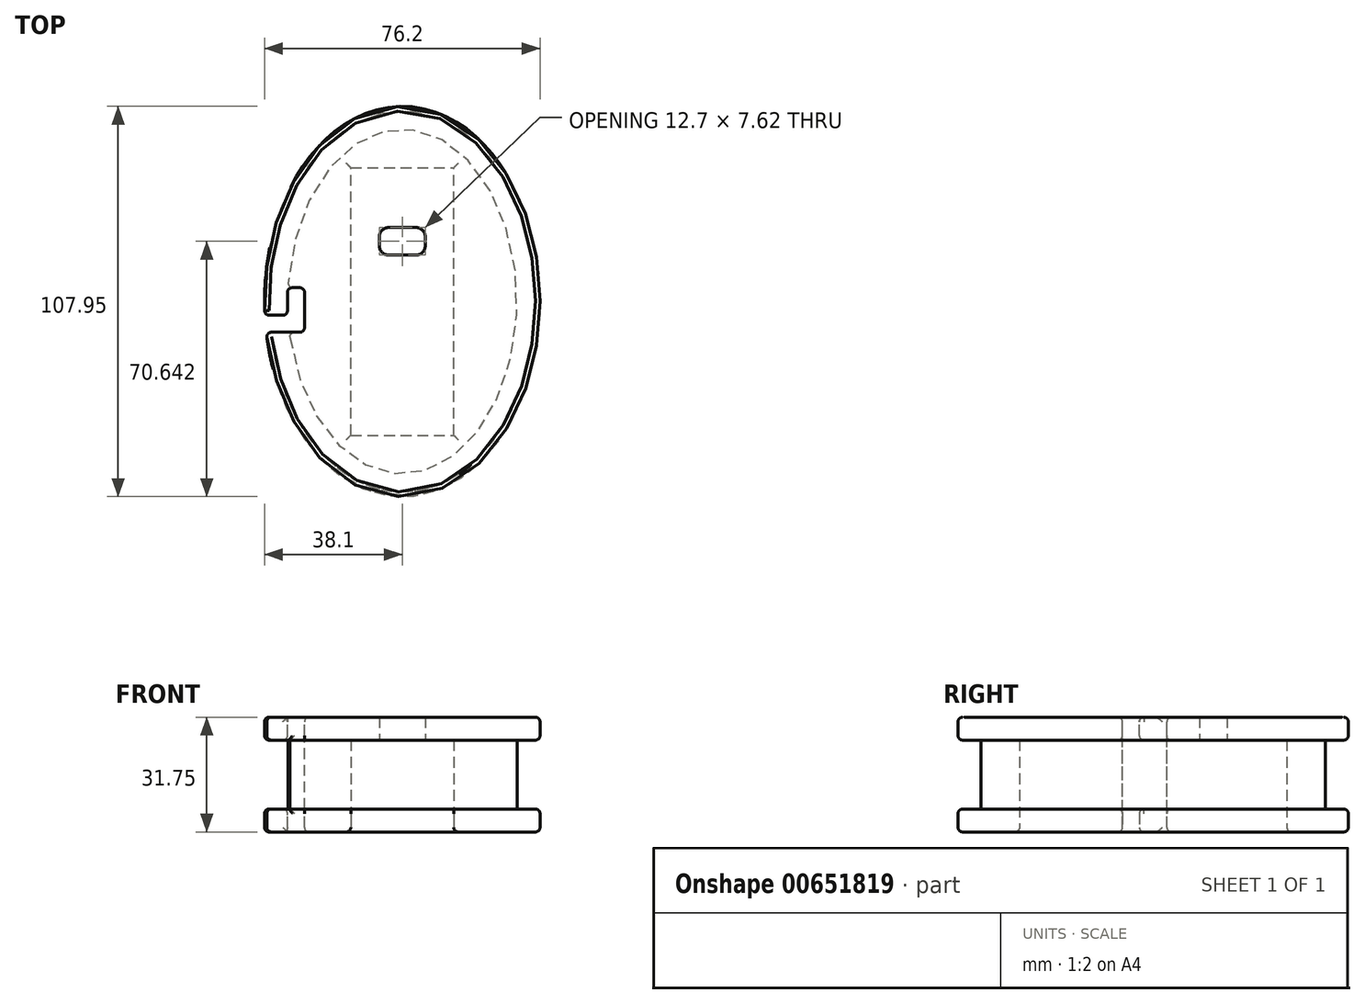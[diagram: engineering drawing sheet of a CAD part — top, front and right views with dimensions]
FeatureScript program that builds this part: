
annotation { "Feature Type Name" : "Feature", "Feature Type Description" : "" }
export const myFeature = defineFeature(function(context is Context, id is Id, definition is map)
    precondition{}
    {
        {
            var Q0;
            Q0=qCreatedBy(makeId("Top.planeOp"),FACE);
            var sketch = newSketch(context, id + "F0", { "sketchPlane" : qUnion([Q0])});
            skLineSegment(sketch, "E0.bottom", {"start": v(-14.24, -36.98) * mm, "end": v(14.24, -36.98) * mm});
            skLineSegment(sketch, "E0.top", {"start": v(-14.24, 36.98) * mm, "end": v(14.24, 36.98) * mm});
            skLineSegment(sketch, "E0.left", {"start": v(-14.24, -36.98) * mm, "end": v(-14.24, 36.98) * mm});
            skLineSegment(sketch, "E0.right", {"start": v(14.24, -36.98) * mm, "end": v(14.24, 36.98) * mm});
            skEllipse(sketch, "E1", {"center": v(0, 0) * mm, "majorRadius": 47.63 * mm, "minorRadius": 31.75 * mm, "majorAxis": v(0, 1)});
            skSolve(sketch);
        }
        {
            var Q0;
            Q0=makeQuery(id+"F0.imprint","IMPRINT",FACE,{"disambiguationData":[TD([[makeQuery(id+"F0.imprint","IMPRINT",EDGE,{"derivedFrom":sQuery(id+"F0.wireOp",EDGE,"E0.bottom")}),-1.0]])]});
            extrude(context, id + "F1", {"entities" : qUnion([Q0]), "depth" : 25.4 * mm, "offsetDistance" : 25.4 * mm});
        }
        {
            var Q0;
            Q0=makeQuery(id+"F1.opExtrude","CAP_FACE",FACE,{"disambiguationData":[OSD([sQuery(id+"F0.wireOp",EDGE,"E0.bottom"),sQuery(id+"F0.wireOp",EDGE,"E0.top"),sQuery(id+"F0.wireOp",EDGE,"E0.left"),sQuery(id+"F0.wireOp",EDGE,"E0.right"),sQuery(id+"F0.wireOp",EDGE,"E1")])],"isStart":false});
            var sketch = newSketch(context, id + "F2", { "sketchPlane" : qUnion([Q0])});
            skEllipse(sketch, "E2", {"center": v(0, 0) * mm, "majorRadius": 53.98 * mm, "minorRadius": 38.1 * mm, "majorAxis": v(0, -1)});
            skSolve(sketch);
        }
        {
            var Q0;
            Q0=makeQuery(id+"F2.imprint","IMPRINT",FACE,{"disambiguationData":[TD([[makeQuery(id+"F2.imprint","IMPRINT",EDGE,{"derivedFrom":sQuery(id+"F2.wireOp",EDGE,"E2")}),1.0]])]});
            var Q1;
            Q1=makeQuery(id+"F2.imprint","IMPRINT",FACE,{"disambiguationData":[TD([[makeQuery(id+"F2.imprint","IMPRINT",EDGE,{"derivedFrom":makeQuery(id+"F1.opExtrude","CAP_EDGE",EDGE,{"disambiguationData":[OSD([sQuery(id+"F0.wireOp",EDGE,"E0.bottom")])],"isStart":false})}),-1.0]])]});
            var Q2;
            Q2=makeQuery(id+"F2.imprint","IMPRINT",FACE,{"disambiguationData":[TD([[makeQuery(id+"F2.imprint","IMPRINT",EDGE,{"derivedFrom":makeQuery(id+"F1.opExtrude","CAP_EDGE",EDGE,{"disambiguationData":[OSD([sQuery(id+"F0.wireOp",EDGE,"E0.bottom")])],"isStart":false})}),1.0]])]});
            extrude(context, id + "F3", {"entities" : qUnion([Q0, Q1, Q2]), "operationType" : NewBodyOperationType.ADD, "depth" : 6.35 * mm, "offsetDistance" : 25.4 * mm});
        }
        {
            var Q0;
            Q0=makeQuery(id+"F1.opExtrude","CAP_FACE",FACE,{"disambiguationData":[OSD([sQuery(id+"F0.wireOp",EDGE,"E0.bottom"),sQuery(id+"F0.wireOp",EDGE,"E0.top"),sQuery(id+"F0.wireOp",EDGE,"E0.left"),sQuery(id+"F0.wireOp",EDGE,"E0.right"),sQuery(id+"F0.wireOp",EDGE,"E1")])],"isStart":true});
            var sketch = newSketch(context, id + "F4", { "sketchPlane" : qUnion([Q0])});
            skEllipse(sketch, "E3", {"center": v(0, 0) * mm, "majorRadius": 53.98 * mm, "minorRadius": 38.1 * mm, "majorAxis": v(0, 1)});
            skSolve(sketch);
        }
        {
            var Q0;
            Q0=makeQuery(id+"F4.imprint","IMPRINT",FACE,{"disambiguationData":[TD([[makeQuery(id+"F4.imprint","IMPRINT",EDGE,{"derivedFrom":sQuery(id+"F4.wireOp",EDGE,"E3")}),1.0]])]});
            extrude(context, id + "F5", {"entities" : qUnion([Q0]), "operationType" : NewBodyOperationType.ADD, "oppositeDirection" : true, "depth" : 6.35 * mm, "offsetDistance" : 25.4 * mm});
        }
        {
            var Q0;
            Q0=makeQuery(id+"F5.opExtrude","CAP_EDGE",EDGE,{"disambiguationData":[OSD([sQuery(id+"F4.wireOp",EDGE,"E3")])],"isStart":true});
            var Q1;
            Q1=makeQuery(id+"F5.opExtrude","CAP_EDGE",EDGE,{"disambiguationData":[OSD([sQuery(id+"F4.wireOp",EDGE,"E3")])],"isStart":false});
            var Q2;
            Q2=makeQuery(id+"F3.opExtrude","CAP_EDGE",EDGE,{"disambiguationData":[OSD([sQuery(id+"F2.wireOp",EDGE,"E2")])],"isStart":true});
            var Q3;
            Q3=makeQuery(id+"F3.opExtrude","CAP_EDGE",EDGE,{"disambiguationData":[OSD([sQuery(id+"F2.wireOp",EDGE,"E2")])],"isStart":false});
            fillet(context, id + "F6", {"entities" : qUnion([Q0, Q1, Q2, Q3]), "radius" : 1.27 * mm, "tangentPropagation" : true, "allowEdgeOverflow" : false});
        }
        {
            var Q0;
            Q0=makeQuery(id+"F1.opExtrude","CAP_EDGE",EDGE,{"disambiguationData":[OSD([sQuery(id+"F0.wireOp",EDGE,"E0.left")])],"isStart":true});
            var Q1;
            Q1=makeQuery(id+"F1.opExtrude","CAP_EDGE",EDGE,{"disambiguationData":[OSD([sQuery(id+"F0.wireOp",EDGE,"E0.bottom")])],"isStart":true});
            var Q2;
            Q2=makeQuery(id+"F1.opExtrude","CAP_EDGE",EDGE,{"disambiguationData":[OSD([sQuery(id+"F0.wireOp",EDGE,"E0.right")])],"isStart":true});
            var Q3;
            Q3=makeQuery(id+"F1.opExtrude","CAP_EDGE",EDGE,{"disambiguationData":[OSD([sQuery(id+"F0.wireOp",EDGE,"E0.top")])],"isStart":true});
            fillet(context, id + "F7", {"entities" : qUnion([Q0, Q1, Q2, Q3]), "radius" : 1.27 * mm, "tangentPropagation" : true, "allowEdgeOverflow" : false});
        }
        {
            var Q0;
            Q0=makeQuery(id+"F3.opExtrude","CAP_FACE",FACE,{"disambiguationData":[OSD([sQuery(id+"F2.wireOp",EDGE,"E2")])],"isStart":false});
            var sketch = newSketch(context, id + "F8", { "sketchPlane" : qUnion([Q0])});
            skLineSegment(sketch, "E4", {"start": v(-42.58, -3.81) * mm, "end": v(-31.75, -3.81) * mm});
            skLineSegment(sketch, "E5", {"start": v(-31.75, -3.81) * mm, "end": v(-31.75, 3.81) * mm});
            skLineSegment(sketch, "E6", {"start": v(-31.75, 3.81) * mm, "end": v(-27.05, 3.81) * mm});
            skLineSegment(sketch, "E7", {"start": v(-27.05, 3.81) * mm, "end": v(-27.05, -8.5) * mm});
            skLineSegment(sketch, "E8", {"start": v(-27.05, -8.5) * mm, "end": v(-42.58, -8.5) * mm});
            skLineSegment(sketch, "E9", {"start": v(-42.58, -8.5) * mm, "end": v(-42.58, -3.81) * mm});
            skSolve(sketch);
        }
        {
            var Q0;
            {var subQ1=sQuery(id+"F8.wireOp",EDGE,"E5");Q0=makeQuery(id+"F8.imprint","IMPRINT",FACE,{"disambiguationData":[TD([[makeQuery(id+"F8.imprint","IMPRINT",EDGE,{"derivedFrom":subQ1}),-1.0]])]});}
            var Q1;
            {var subQ0=sQuery(id+"F8.wireOp",EDGE,"E9");Q1=makeQuery(id+"F8.imprint","IMPRINT",FACE,{"disambiguationData":[TD([[makeQuery(id+"F8.imprint","IMPRINT",EDGE,{"derivedFrom":subQ0}),-1.0]])]});}
            extrude(context, id + "F9", {"entities" : qUnion([Q0, Q1]), "operationType" : NewBodyOperationType.REMOVE, "oppositeDirection" : true, "depth" : 31.75 * mm, "offsetDistance" : 25.4 * mm});
        }
        {
            var Q0;
            Q0=makeQuery(id+"F9.boolean.opBoolean","COPY",EDGE,{"derivedFrom":makeQuery(id+"F9.opExtrude","SWEPT_EDGE",EDGE,{"disambiguationData":[OSD([sQuery(id+"F8.wireOp",EDGE,"E6"),sQuery(id+"F8.wireOp",EDGE,"E7")])]})});
            var Q1;
            Q1=makeQuery(id+"F9.boolean.opBoolean","COPY",EDGE,{"derivedFrom":makeQuery(id+"F9.opExtrude","SWEPT_EDGE",EDGE,{"disambiguationData":[OSD([sQuery(id+"F8.wireOp",EDGE,"E7"),sQuery(id+"F8.wireOp",EDGE,"E8")])]})});
            var Q2;
            Q2=makeQuery(id+"F9.boolean.opBoolean","INTERSECT",EDGE,{"derivedFrom":[makeQuery(id+"F1.opExtrude","SWEPT_FACE",FACE,{"disambiguationData":[OSD([sQuery(id+"F0.wireOp",EDGE,"E1")])]}),makeQuery(id+"F9.opExtrude","SWEPT_FACE",FACE,{"disambiguationData":[OSD([sQuery(id+"F8.wireOp",EDGE,"E8")])]})]});
            var Q3;
            Q3=makeQuery(id+"F9.boolean.opBoolean","INTERSECT",EDGE,{"derivedFrom":[makeQuery(id+"F1.opExtrude","SWEPT_FACE",FACE,{"disambiguationData":[OSD([sQuery(id+"F0.wireOp",EDGE,"E1")])]}),makeQuery(id+"F9.opExtrude","SWEPT_FACE",FACE,{"disambiguationData":[OSD([sQuery(id+"F8.wireOp",EDGE,"E6")])]})]});
            fillet(context, id + "F10", {"entities" : qUnion([Q0, Q1, Q2, Q3]), "radius" : 1.27 * mm, "tangentPropagation" : true, "allowEdgeOverflow" : false});
        }
        {
            var Q0;
            {var subQ0=sQuery(id+"F4.wireOp",EDGE,"E3");var subQ1=sQuery(id+"F0.wireOp",EDGE,"E1");var subQ2=sQuery(id+"F8.wireOp",EDGE,"E4");var subQ3=sQuery(id+"F8.wireOp",EDGE,"E5");Q0=makeQuery(id+"F9.boolean.opBoolean","COPY",EDGE,{"disambiguationData":[TD([makeQuery(id+"F5.opExtrude","CAP_FACE",FACE,{"disambiguationData":[OSD([subQ1,subQ0])],"isStart":true})])],"derivedFrom":makeQuery(id+"F9.opExtrude","SWEPT_EDGE",EDGE,{"disambiguationData":[OSD([subQ2,subQ3])]})});}
            var Q1;
            {var subQ0=sQuery(id+"F2.wireOp",EDGE,"E2");var subQ1=sQuery(id+"F8.wireOp",EDGE,"E4");var subQ2=sQuery(id+"F8.wireOp",EDGE,"E5");Q1=makeQuery(id+"F9.boolean.opBoolean","COPY",EDGE,{"disambiguationData":[TD([makeQuery(id+"F3.opExtrude","CAP_FACE",FACE,{"disambiguationData":[OSD([subQ0])],"isStart":true})])],"derivedFrom":makeQuery(id+"F9.opExtrude","SWEPT_EDGE",EDGE,{"disambiguationData":[OSD([subQ1,subQ2])]})});}
            var Q2;
            {var subQ0=sQuery(id+"F2.wireOp",EDGE,"E2");var subQ1=sQuery(id+"F8.wireOp",EDGE,"E5");var subQ2=sQuery(id+"F8.wireOp",EDGE,"E6");Q2=makeQuery(id+"F9.boolean.opBoolean","COPY",EDGE,{"disambiguationData":[TD([makeQuery(id+"F3.opExtrude","CAP_FACE",FACE,{"disambiguationData":[OSD([subQ0])],"isStart":true})])],"derivedFrom":makeQuery(id+"F9.opExtrude","SWEPT_EDGE",EDGE,{"disambiguationData":[OSD([subQ1,subQ2])]})});}
            var Q3;
            {var subQ0=sQuery(id+"F4.wireOp",EDGE,"E3");var subQ1=sQuery(id+"F0.wireOp",EDGE,"E1");var subQ2=sQuery(id+"F8.wireOp",EDGE,"E5");var subQ3=sQuery(id+"F8.wireOp",EDGE,"E6");Q3=makeQuery(id+"F9.boolean.opBoolean","COPY",EDGE,{"disambiguationData":[TD([makeQuery(id+"F5.opExtrude","CAP_FACE",FACE,{"disambiguationData":[OSD([subQ1,subQ0])],"isStart":true})])],"derivedFrom":makeQuery(id+"F9.opExtrude","SWEPT_EDGE",EDGE,{"disambiguationData":[OSD([subQ2,subQ3])]})});}
            var Q4;
            Q4=makeQuery(id+"F9.boolean.opBoolean","INTERSECT",EDGE,{"derivedFrom":[makeQuery(id+"F3.opExtrude","SWEPT_FACE",FACE,{"disambiguationData":[OSD([sQuery(id+"F2.wireOp",EDGE,"E2")])]}),makeQuery(id+"F9.opExtrude","SWEPT_FACE",FACE,{"disambiguationData":[OSD([sQuery(id+"F8.wireOp",EDGE,"E8")])]})]});
            var Q5;
            Q5=makeQuery(id+"F9.boolean.opBoolean","INTERSECT",EDGE,{"derivedFrom":[makeQuery(id+"F5.opExtrude","SWEPT_FACE",FACE,{"disambiguationData":[OSD([sQuery(id+"F4.wireOp",EDGE,"E3")])]}),makeQuery(id+"F9.opExtrude","SWEPT_FACE",FACE,{"disambiguationData":[OSD([sQuery(id+"F8.wireOp",EDGE,"E8")])]})]});
            var Q6;
            Q6=makeQuery(id+"F9.boolean.opBoolean","INTERSECT",EDGE,{"derivedFrom":[makeQuery(id+"F5.opExtrude","SWEPT_FACE",FACE,{"disambiguationData":[OSD([sQuery(id+"F4.wireOp",EDGE,"E3")])]}),makeQuery(id+"F9.opExtrude","SWEPT_FACE",FACE,{"disambiguationData":[OSD([sQuery(id+"F8.wireOp",EDGE,"E4")])]})]});
            var Q7;
            Q7=makeQuery(id+"F9.boolean.opBoolean","INTERSECT",EDGE,{"derivedFrom":[makeQuery(id+"F3.opExtrude","SWEPT_FACE",FACE,{"disambiguationData":[OSD([sQuery(id+"F2.wireOp",EDGE,"E2")])]}),makeQuery(id+"F9.opExtrude","SWEPT_FACE",FACE,{"disambiguationData":[OSD([sQuery(id+"F8.wireOp",EDGE,"E4")])]})]});
            fillet(context, id + "F11", {"entities" : qUnion([Q0, Q1, Q2, Q3, Q4, Q5, Q6, Q7]), "radius" : 1.27 * mm, "tangentPropagation" : true, "allowEdgeOverflow" : false});
        }
        {
            var Q0;
            Q0=makeQuery(id+"F9.boolean.opBoolean","INTERSECT",EDGE,{"derivedFrom":[makeQuery(id+"F5.opExtrude","CAP_FACE",FACE,{"disambiguationData":[OSD([sQuery(id+"F0.wireOp",EDGE,"E1"),sQuery(id+"F4.wireOp",EDGE,"E3")])],"isStart":false}),makeQuery(id+"F9.opExtrude","SWEPT_FACE",FACE,{"disambiguationData":[OSD([sQuery(id+"F8.wireOp",EDGE,"E5")])]})]});
            var Q1;
            {var subQ0=sQuery(id+"F2.wireOp",EDGE,"E2");Q1=makeQuery(id+"F9.boolean.opBoolean","INTERSECT",EDGE,{"derivedFrom":[makeQuery(id+"F3.boolean.opBoolean","SPLIT",FACE,{"disambiguationData":[TD([makeQuery(id+"F1.opExtrude","SWEPT_FACE",FACE,{"disambiguationData":[OSD([sQuery(id+"F0.wireOp",EDGE,"E1")])]})])],"derivedFrom":makeQuery(id+"F3.opExtrude","CAP_FACE",FACE,{"disambiguationData":[OSD([subQ0])],"isStart":true})}),makeQuery(id+"F9.opExtrude","SWEPT_FACE",FACE,{"disambiguationData":[OSD([sQuery(id+"F8.wireOp",EDGE,"E5")])]})]});}
            fillet(context, id + "F12", {"entities" : qUnion([Q0, Q1]), "radius" : 1.27 * mm, "tangentPropagation" : true, "allowEdgeOverflow" : false});
        }
        {
            var Q0;
            Q0=makeQuery(id+"F3.boolean.opBoolean","SPLIT",FACE,{"disambiguationData":[TD([makeQuery(id+"F1.opExtrude","SWEPT_FACE",FACE,{"disambiguationData":[OSD([sQuery(id+"F0.wireOp",EDGE,"E0.bottom")])]})])],"derivedFrom":makeQuery(id+"F3.opExtrude","CAP_FACE",FACE,{"disambiguationData":[OSD([sQuery(id+"F2.wireOp",EDGE,"E2")])],"isStart":true})});
            var sketch = newSketch(context, id + "F13", { "sketchPlane" : qUnion([Q0])});
            skLineSegment(sketch, "E10.bottom", {"start": v(-6.35, -12.85) * mm, "end": v(6.35, -12.85) * mm});
            skLineSegment(sketch, "E10.top", {"start": v(-6.35, -20.47) * mm, "end": v(6.35, -20.47) * mm});
            skLineSegment(sketch, "E10.left", {"start": v(-6.35, -12.85) * mm, "end": v(-6.35, -20.47) * mm});
            skLineSegment(sketch, "E10.right", {"start": v(6.35, -12.85) * mm, "end": v(6.35, -20.47) * mm});
            skSolve(sketch);
        }
        {
            var Q0;
            Q0=makeQuery(id+"F13.imprint","IMPRINT",FACE,{"disambiguationData":[TD([[makeQuery(id+"F13.imprint","IMPRINT",EDGE,{"derivedFrom":sQuery(id+"F13.wireOp",EDGE,"E10.bottom")}),-1.0]])]});
            extrude(context, id + "F14", {"entities" : qUnion([Q0]), "operationType" : NewBodyOperationType.REMOVE, "endBound" : BoundingType.THROUGH_ALL, "oppositeDirection" : true, "depth" : 25.4 * mm, "offsetDistance" : 25.4 * mm});
        }
        {
            var Q0;
            Q0=makeQuery(id+"F14.boolean.opBoolean","COPY",EDGE,{"derivedFrom":makeQuery(id+"F14.opExtrude","SWEPT_EDGE",EDGE,{"disambiguationData":[OSD([sQuery(id+"F13.wireOp",EDGE,"E10.bottom"),sQuery(id+"F13.wireOp",EDGE,"E10.right")])]})});
            var Q1;
            Q1=makeQuery(id+"F14.boolean.opBoolean","COPY",EDGE,{"derivedFrom":makeQuery(id+"F14.opExtrude","SWEPT_EDGE",EDGE,{"disambiguationData":[OSD([sQuery(id+"F13.wireOp",EDGE,"E10.bottom"),sQuery(id+"F13.wireOp",EDGE,"E10.left")])]})});
            var Q2;
            Q2=makeQuery(id+"F14.boolean.opBoolean","COPY",EDGE,{"derivedFrom":makeQuery(id+"F14.opExtrude","SWEPT_EDGE",EDGE,{"disambiguationData":[OSD([sQuery(id+"F13.wireOp",EDGE,"E10.top"),sQuery(id+"F13.wireOp",EDGE,"E10.left")])]})});
            var Q3;
            Q3=makeQuery(id+"F14.boolean.opBoolean","COPY",EDGE,{"derivedFrom":makeQuery(id+"F14.opExtrude","SWEPT_EDGE",EDGE,{"disambiguationData":[OSD([sQuery(id+"F13.wireOp",EDGE,"E10.top"),sQuery(id+"F13.wireOp",EDGE,"E10.right")])]})});
            fillet(context, id + "F15", {"entities" : qUnion([Q0, Q1, Q2, Q3]), "radius" : 2.54 * mm, "tangentPropagation" : true, "allowEdgeOverflow" : false});
        }
    });
